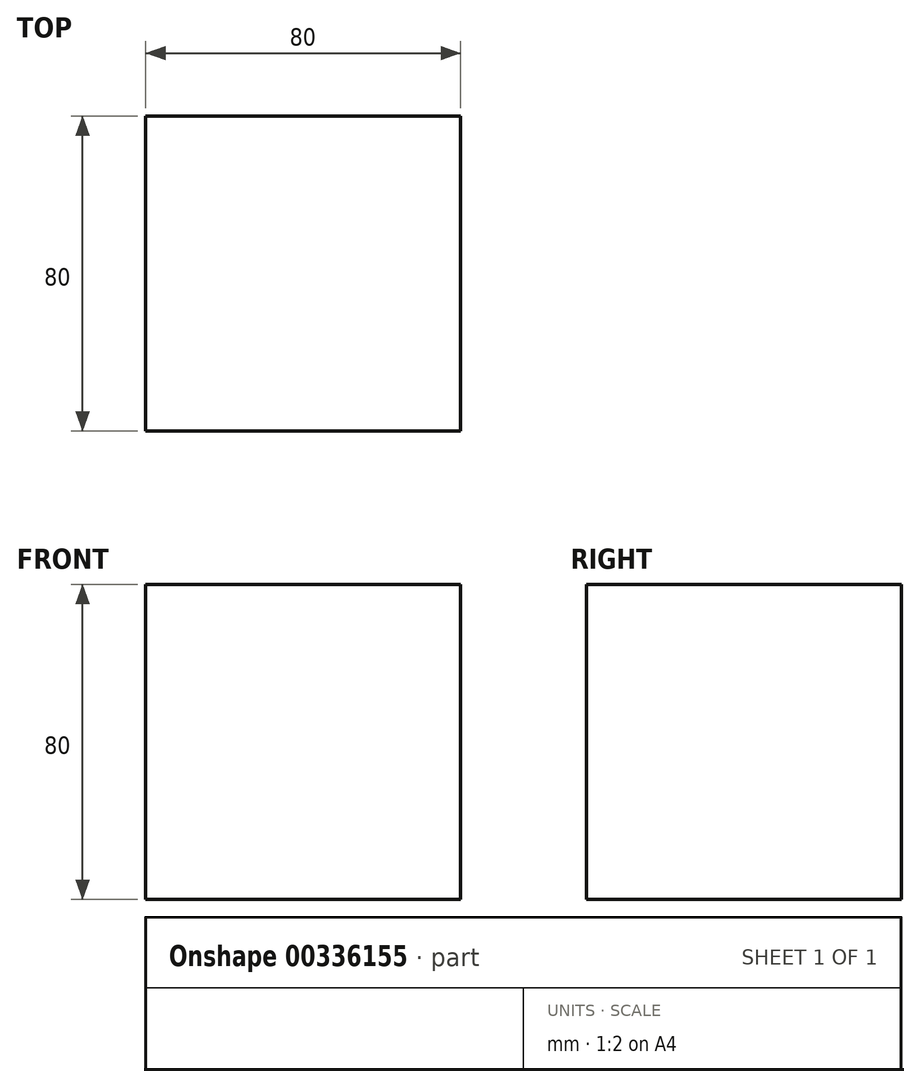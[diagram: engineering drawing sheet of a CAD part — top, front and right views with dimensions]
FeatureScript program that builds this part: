
annotation { "Feature Type Name" : "Feature", "Feature Type Description" : "" }
export const myFeature = defineFeature(function(context is Context, id is Id, definition is map)
    precondition{}
    {
        {
            var Q0;
            Q0=qCreatedBy(makeId("Top.planeOp"),FACE);
            var sketch = newSketch(context, id + "F0", { "sketchPlane" : qUnion([Q0])});
            skLineSegment(sketch, "E0.bottom", {"start": v(40, 40) * mm, "end": v(-40, 40) * mm});
            skLineSegment(sketch, "E0.top", {"start": v(40, -40) * mm, "end": v(-40, -40) * mm});
            skLineSegment(sketch, "E0.left", {"start": v(40, 40) * mm, "end": v(40, -40) * mm});
            skLineSegment(sketch, "E0.right", {"start": v(-40, 40) * mm, "end": v(-40, -40) * mm});
            skPoint(sketch, "E0.middle", {"position": v(0, 0) * mm});
            skSolve(sketch);
        }
        {
            var Q0;
            Q0=makeQuery(id+"F0.imprint","IMPRINT",FACE,{"disambiguationData":[TD([[makeQuery(id+"F0.imprint","IMPRINT",EDGE,{"derivedFrom":sQuery(id+"F0.wireOp",EDGE,"E0.bottom")}),1.0]])]});
            extrude(context, id + "F1", {"entities" : qUnion([Q0]), "depth" : 80 * mm});
        }
    });
